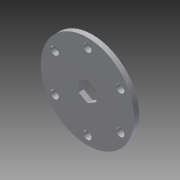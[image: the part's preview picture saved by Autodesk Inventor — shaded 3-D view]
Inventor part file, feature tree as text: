
AUTODESK INVENTOR PART (.ipt)
format: ipt  version: 2014 SP1 (Build 180222100, 222)  size: 118,784 bytes
history: native  units: in
note: dims shown in document units (in); Inventor stores cm internally (conversion verified against a paired STEP export)
features: extrude x1, sketch x1
ambient origin geometry x8: Origin, YZ Plane, XZ Plane, XY Plane, X Axis, Y Axis, Z Axis, Center Point
bodies: Solid1 (feature_tree)
feature tree (2):
  extrude  "Extrusion1"  Depth=0.125in TaperAngle=0.0deg
  sketch  "Sketch1"  dims[d0=0.5in d1=0.125in d2=0.0in]
